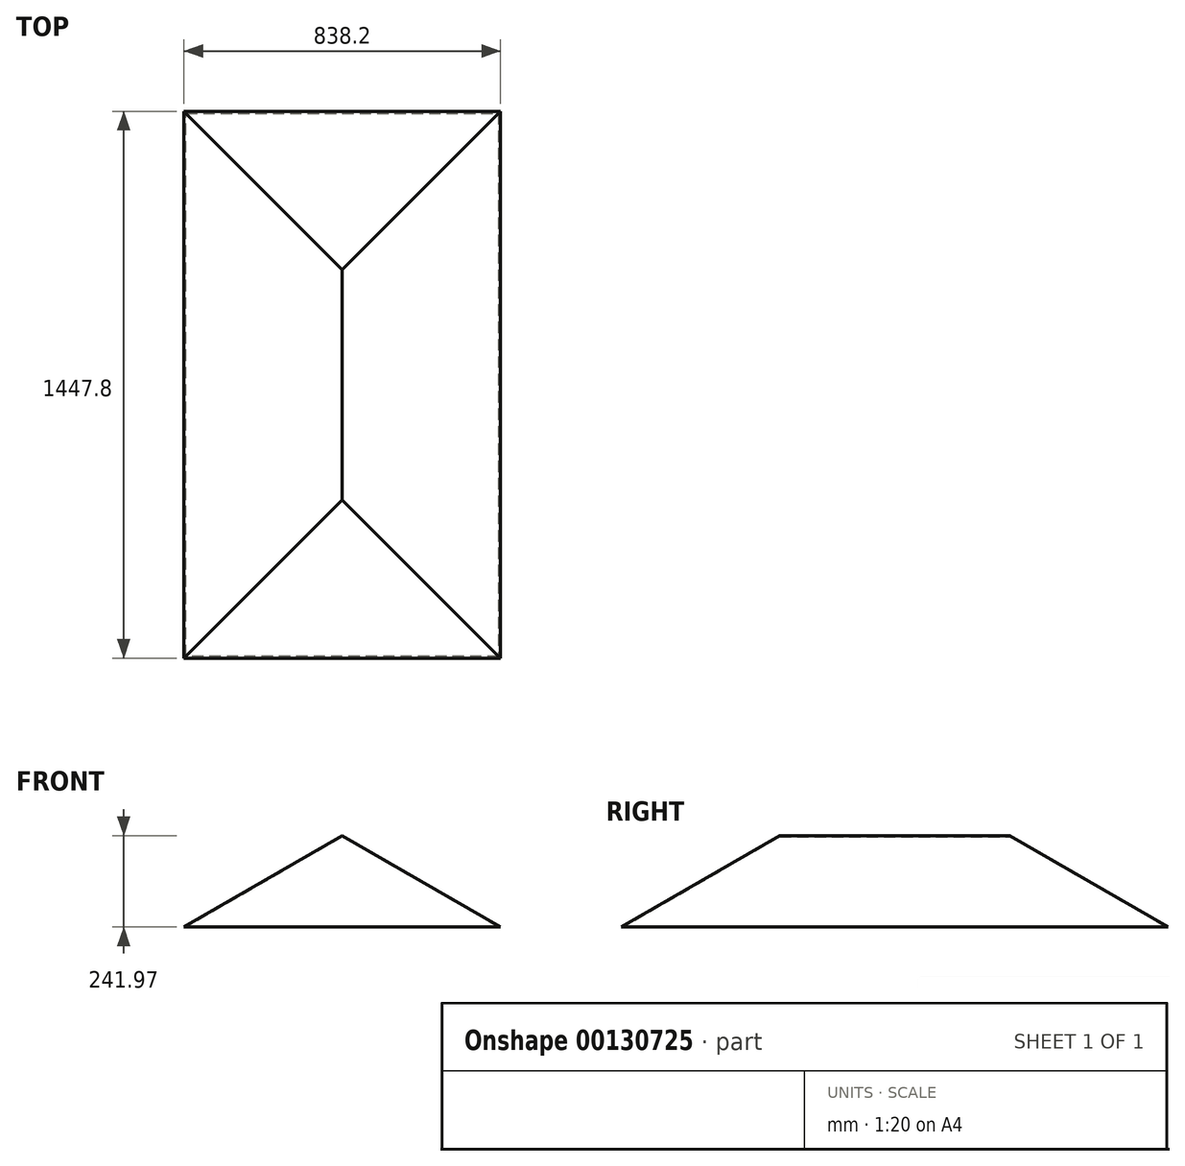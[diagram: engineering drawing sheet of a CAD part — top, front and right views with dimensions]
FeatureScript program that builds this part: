
annotation { "Feature Type Name" : "Feature", "Feature Type Description" : "" }
export const myFeature = defineFeature(function(context is Context, id is Id, definition is map)
    precondition{}
    {
        {
            var Q0;
            Q0=qCreatedBy(makeId("Top.planeOp"),FACE);
            var sketch = newSketch(context, id + "F0", { "sketchPlane" : qUnion([Q0])});
            skLineSegment(sketch, "E0.bottom", {"start": v(419.1, 723.9) * mm, "end": v(-419.1, 723.9) * mm});
            skLineSegment(sketch, "E0.top", {"start": v(419.1, -723.9) * mm, "end": v(-419.1, -723.9) * mm});
            skLineSegment(sketch, "E0.left", {"start": v(419.1, 723.9) * mm, "end": v(419.1, -723.9) * mm});
            skLineSegment(sketch, "E0.right", {"start": v(-419.1, 723.9) * mm, "end": v(-419.1, -723.9) * mm});
            skPoint(sketch, "E0.middle", {"position": v(0, 0) * mm});
            skSolve(sketch);
        }
        {
            var Q0;
            Q0 = qSketchRegion(id + "F0", true);
            extrude(context, id + "F1", {"entities" : qUnion([Q0]), "depth" : 304.8 * mm, "hasDraft" : true, "draftAngle" : 60 * degree, "draftPullDirection" : true});
        }
        {
            var Q0;
            Q0=makeQuery(id+"F1.opExtrude","CAP_FACE",FACE,{"disambiguationData":[OSD([sQuery(id+"F0.wireOp",EDGE,"E0.bottom"),sQuery(id+"F0.wireOp",EDGE,"E0.top"),sQuery(id+"F0.wireOp",EDGE,"E0.left"),sQuery(id+"F0.wireOp",EDGE,"E0.right")])],"isStart":true});
            shell(context, id + "F2", {"entities" : qUnion([Q0]), "thickness" : 2.54 * mm});
        }
    });
